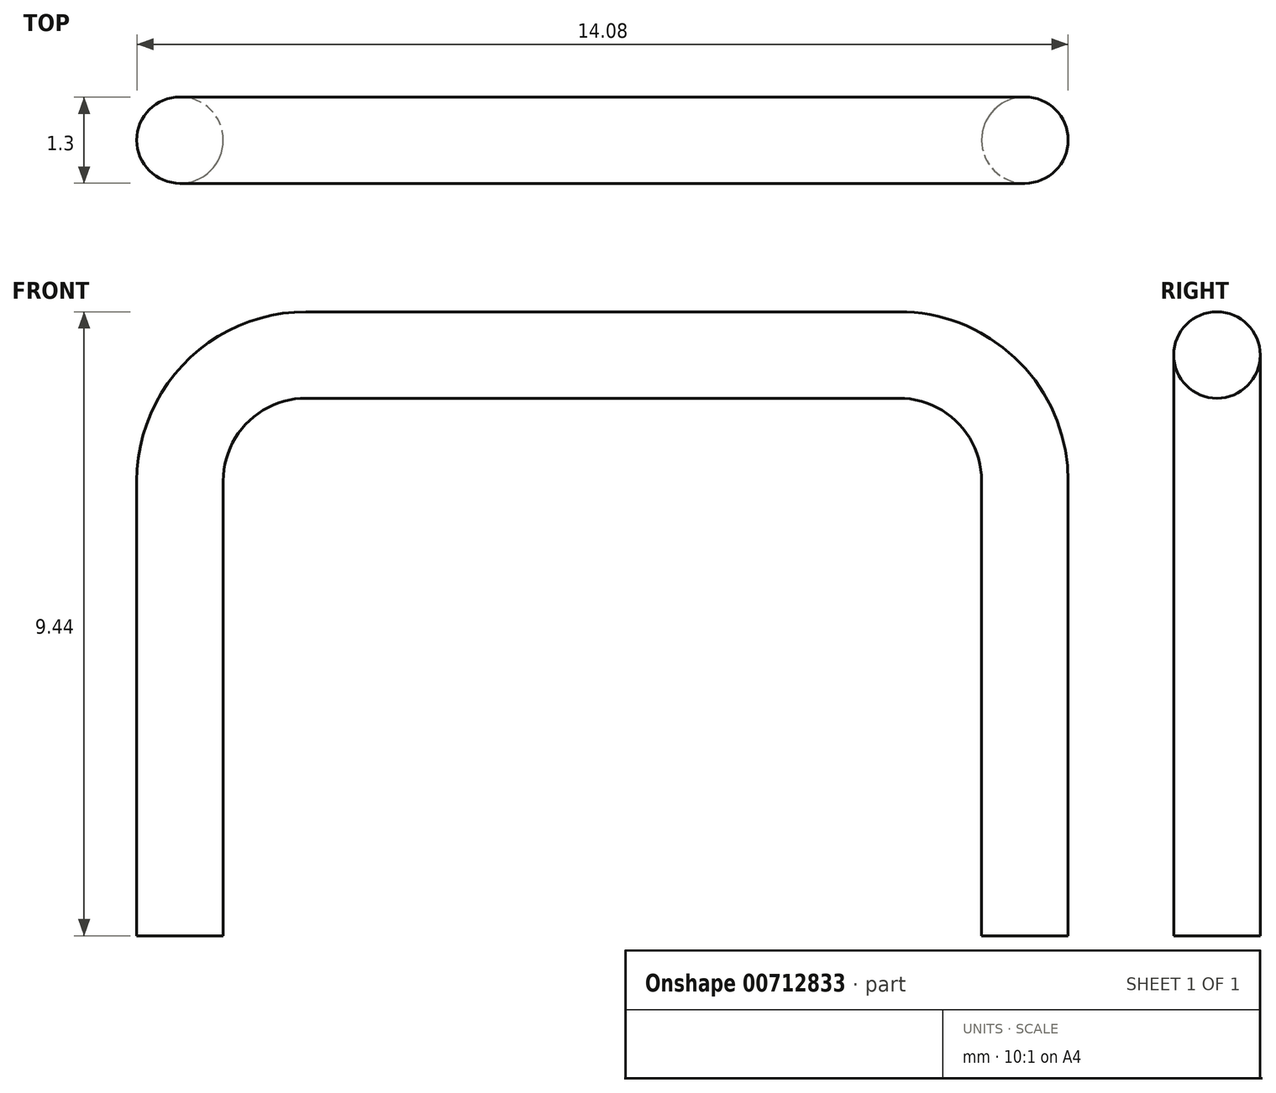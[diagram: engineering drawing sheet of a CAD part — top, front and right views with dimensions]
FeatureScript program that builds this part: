
annotation { "Feature Type Name" : "Feature", "Feature Type Description" : "" }
export const myFeature = defineFeature(function(context is Context, id is Id, definition is map)
    precondition{}
    {
        {
            var Q0;
            Q0=qCreatedBy(makeId("Front.planeOp"),FACE);
            var sketch = newSketch(context, id + "F0", { "sketchPlane" : qUnion([Q0])});
            skLineSegment(sketch, "E0", {"start": v(0, 0) * mm, "end": v(0, 6.88) * mm});
            skLineSegment(sketch, "E1", {"start": v(12.78, 0) * mm, "end": v(12.78, 6.88) * mm});
            skLineSegment(sketch, "E2", {"start": v(1.9, 8.79) * mm, "end": v(10.87, 8.79) * mm});
            skPoint(sketch, "E3.visualSharp", {"position": v(0, 8.79) * mm});
            skArc(sketch, "E3.filletArc", {"start": v(1.9, 8.79) * mm, "mid": v(0.56, 8.23) * mm, "end": v(0, 6.88) * mm});
            skPoint(sketch, "E4.visualSharp", {"position": v(12.78, 8.79) * mm});
            skArc(sketch, "E4.filletArc", {"start": v(12.78, 6.88) * mm, "mid": v(12.22, 8.23) * mm, "end": v(10.87, 8.79) * mm});
            skSolve(sketch);
        }
        {
            var Q0;
            Q0=sQuery(id+"F0.wireOp",VERTEX,"E0.start");
            var Q1;
            Q1=qCreatedBy(makeId("Top.planeOp"),FACE);
            cPlane(context, id + "F1", {"entities" : qUnion([Q0, Q1]), "cplaneType" : CPlaneType.PLANE_POINT, "offset" : 25.4 * mm, "width" : 152.4 * mm, "height" : 152.4 * mm});
        }
        {
            var Q0;
            Q0=qCreatedBy(id+"F1.planeOp",FACE);
            var sketch = newSketch(context, id + "F2", { "sketchPlane" : qUnion([Q0])});
            skCircle(sketch, "E5", {"center": v(0, 0) * mm, "radius": 0.65 * mm});
            skSolve(sketch);
        }
        {
            var Q0;
            Q0=makeQuery(id+"F2.imprint","IMPRINT",FACE,{"disambiguationData":[TD([[makeQuery(id+"F2.imprint","IMPRINT",EDGE,{"derivedFrom":sQuery(id+"F2.wireOp",EDGE,"E5")}),1.0]])]});
            var Q1;
            Q1=sQuery(id+"F0.wireOp",EDGE,"E0");
            var Q2;
            Q2=sQuery(id+"F0.wireOp",EDGE,"E3.filletArc");
            var Q3;
            Q3=sQuery(id+"F0.wireOp",EDGE,"E2");
            var Q4;
            Q4=sQuery(id+"F0.wireOp",EDGE,"E4.filletArc");
            var Q5;
            Q5=sQuery(id+"F0.wireOp",EDGE,"E1");
            sweep(context, id + "F3", {"profiles" : qUnion([Q0]), "path" : qUnion([Q1, Q2, Q3, Q4, Q5])});
        }
    });
